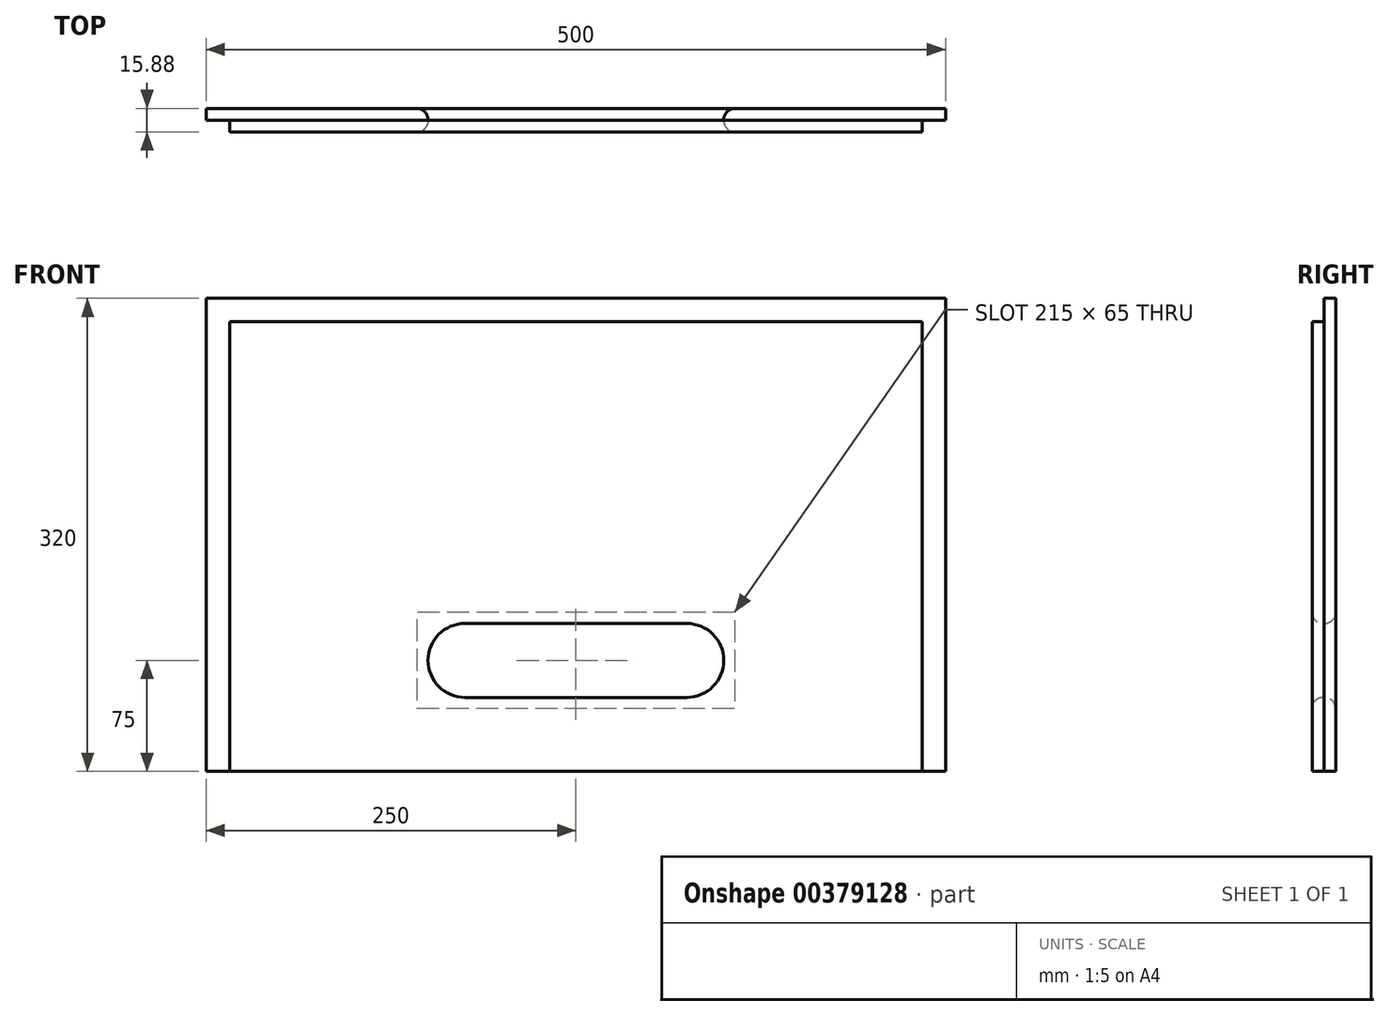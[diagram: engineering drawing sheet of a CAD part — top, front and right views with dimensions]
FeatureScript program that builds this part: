
annotation { "Feature Type Name" : "Feature", "Feature Type Description" : "" }
export const myFeature = defineFeature(function(context is Context, id is Id, definition is map)
    precondition{}
    {
        {
            var Q0;
            Q0=qCreatedBy(makeId("Front.planeOp"),FACE);
            var sketch = newSketch(context, id + "F0", { "sketchPlane" : qUnion([Q0])});
            skLineSegment(sketch, "E0.bottom", {"start": v(526, -160) * mm, "end": v(26, -160) * mm});
            skLineSegment(sketch, "E0.top", {"start": v(526, 160) * mm, "end": v(26, 160) * mm});
            skLineSegment(sketch, "E0.left", {"start": v(526, -160) * mm, "end": v(526, 160) * mm});
            skLineSegment(sketch, "E0.right", {"start": v(26, -160) * mm, "end": v(26, 160) * mm});
            skPoint(sketch, "E0.middle", {"position": v(0, 0) * mm});
            skLineSegment(sketch, "E1.bottom", {"start": v(351, -110) * mm, "end": v(201, -110) * mm});
            skLineSegment(sketch, "E1.top", {"start": v(351, -60) * mm, "end": v(201, -60) * mm});
            skLineSegment(sketch, "E1.left", {"start": v(351, -110) * mm, "end": v(351, -60) * mm});
            skLineSegment(sketch, "E1.right", {"start": v(201, -110) * mm, "end": v(201, -60) * mm});
            skPoint(sketch, "E2", {"position": v(201, -85) * mm});
            skPoint(sketch, "E3", {"position": v(351, -85) * mm});
            skPoint(sketch, "E4", {"position": v(276, -160) * mm});
            skPoint(sketch, "E5", {"position": v(276, -110) * mm});
            skCircle(sketch, "E6", {"center": v(201, -85) * mm, "radius": 25 * mm});
            skCircle(sketch, "E7", {"center": v(351, -85) * mm, "radius": 25 * mm});
            skSolve(sketch);
        }
        {
            var Q0;
            Q0=makeQuery(id+"F0.imprint","IMPRINT",FACE,{"disambiguationData":[TD([[makeQuery(id+"F0.imprint","IMPRINT",EDGE,{"derivedFrom":sQuery(id+"F0.wireOp",EDGE,"E0.bottom")}),-1.0]])]});
            var Q1;
            Q1 = qSketchRegion(id + "F0", true);
            extrude(context, id + "F1", {"entities" : qUnion([Q0, Q1]), "depth" : 15.88 * mm});
        }
        {
            var Q0;
            Q0=makeQuery(id+"F1.opExtrude","SWEPT_FACE",FACE,{"disambiguationData":[OSD([sQuery(id+"F0.wireOp",EDGE,"E0.bottom")])]});
            var sketch = newSketch(context, id + "F2", { "sketchPlane" : qUnion([Q0])});
            skLineSegment(sketch, "E8.bottom", {"start": v(26, 15.88) * mm, "end": v(41.88, 15.88) * mm});
            skLineSegment(sketch, "E8.top", {"start": v(26, 7.94) * mm, "end": v(41.88, 7.94) * mm});
            skLineSegment(sketch, "E8.left", {"start": v(26, 15.88) * mm, "end": v(26, 7.94) * mm});
            skLineSegment(sketch, "E8.right", {"start": v(41.88, 15.88) * mm, "end": v(41.88, 7.94) * mm});
            skLineSegment(sketch, "E9.bottom", {"start": v(526, 15.88) * mm, "end": v(510.12, 15.88) * mm});
            skLineSegment(sketch, "E9.top", {"start": v(526, 7.94) * mm, "end": v(510.12, 7.94) * mm});
            skLineSegment(sketch, "E9.left", {"start": v(526, 15.88) * mm, "end": v(526, 7.94) * mm});
            skLineSegment(sketch, "E9.right", {"start": v(510.12, 15.88) * mm, "end": v(510.12, 7.94) * mm});
            skSolve(sketch);
        }
        {
            var Q0;
            Q0=makeQuery(id+"F2.imprint","IMPRINT",FACE,{"disambiguationData":[TD([[makeQuery(id+"F2.imprint","IMPRINT",EDGE,{"derivedFrom":sQuery(id+"F2.wireOp",EDGE,"E8.bottom")}),1.0]])]});
            var Q1;
            Q1=makeQuery(id+"F2.imprint","IMPRINT",FACE,{"disambiguationData":[TD([[makeQuery(id+"F2.imprint","IMPRINT",EDGE,{"derivedFrom":sQuery(id+"F2.wireOp",EDGE,"E9.bottom")}),1.0]])]});
            extrude(context, id + "F3", {"entities" : qUnion([Q0, Q1]), "operationType" : NewBodyOperationType.REMOVE, "endBound" : BoundingType.THROUGH_ALL, "oppositeDirection" : true, "depth" : 320 * mm});
        }
        {
            var Q0;
            Q0=makeQuery(id+"F3.boolean.opBoolean","COPY",FACE,{"derivedFrom":makeQuery(id+"F3.opExtrude","SWEPT_FACE",FACE,{"disambiguationData":[OSD([sQuery(id+"F2.wireOp",EDGE,"E8.right")])]})});
            var sketch = newSketch(context, id + "F4", { "sketchPlane" : qUnion([Q0])});
            skLineSegment(sketch, "E10.bottom", {"start": v(15.88, 160) * mm, "end": v(7.94, 160) * mm});
            skLineSegment(sketch, "E10.top", {"start": v(15.88, 144.12) * mm, "end": v(7.94, 144.12) * mm});
            skLineSegment(sketch, "E10.left", {"start": v(15.88, 160) * mm, "end": v(15.88, 144.12) * mm});
            skLineSegment(sketch, "E10.right", {"start": v(7.94, 160) * mm, "end": v(7.94, 144.12) * mm});
            skSolve(sketch);
        }
        {
            var Q0;
            Q0=makeQuery(id+"F4.imprint","IMPRINT",FACE,{"disambiguationData":[TD([[makeQuery(id+"F4.imprint","IMPRINT",EDGE,{"derivedFrom":sQuery(id+"F4.wireOp",EDGE,"E10.bottom")}),1.0]])]});
            extrude(context, id + "F5", {"entities" : qUnion([Q0]), "operationType" : NewBodyOperationType.REMOVE, "endBound" : BoundingType.THROUGH_ALL, "oppositeDirection" : true, "depth" : 25 * mm});
        }
        {
            var Q0;
            Q0=makeQuery(id+"F1.opExtrude","CAP_EDGE",EDGE,{"disambiguationData":[OSD([sQuery(id+"F0.wireOp",EDGE,"E1.top")])],"isStart":true});
            var Q1;
            Q1=makeQuery(id+"F1.opExtrude","CAP_EDGE",EDGE,{"disambiguationData":[OSD([sQuery(id+"F0.wireOp",EDGE,"E1.top")])],"isStart":false});
            fillet(context, id + "F6", {"entities" : qUnion([Q0, Q1]), "radius" : 7.5 * mm, "tangentPropagation" : true, "allowEdgeOverflow" : false});
        }
    });
